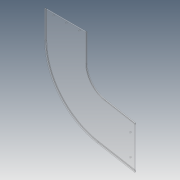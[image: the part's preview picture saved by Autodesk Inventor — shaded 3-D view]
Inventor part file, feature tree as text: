
AUTODESK INVENTOR PART (.ipt)
format: ipt  version: 2012 (Build 160160000, 160)  size: 145,408 bytes
history: native  units: in
note: dims shown in document units (in); Inventor stores cm internally (conversion verified against a paired STEP export)
features: extrude x2, hole x2, pattern_linear x2, sketch x2
ambient origin geometry x8: Origin, YZ Plane, XZ Plane, XY Plane, X Axis, Y Axis, Z Axis, Center Point
bodies: Solid1 (feature_tree)
feature tree (8):
  extrude  "Extrusion1"  Depth=9.625in
  extrude  "Extrusion3"  Depth=5.0in
  hole  "Hole1"  [1 undecoded]
  pattern_linear  "Rectangular Pattern1"  Spacing1=12.5in  [1 undecoded]
  hole  "Hole2"  [1 undecoded]
  pattern_linear  "Rectangular Pattern2"  Spacing1=0.25in  [1 undecoded]
  sketch  "Sketch1"  dims[d0=9.625in d1=9.625in]
  sketch  "Sketch3"  dims[d2=0.6871in d3=5.0in d4=14.625in d5=12.5in d6=20.75in d7=0.25in d8=0.0in d21=0.1875in d23=0.1875in d24=0.1875in d25=0.1875in d26=0.1875in d27=0.1875in d28=0.125in d29=0.125in d30=0.125in d31=0.125in d32=0.125in d33=0.0in d34=1.125in d35=14.875in d36=0.265in d37=0.75in d38=0.375in d39=0.25in d40=0.5635in d41=1.0in d42=0.8108in d43=0.7874in d45=5.0in d46=0.5in d47=1.75in d48=0.265in d49=0.75in d50=0.375in d51=0.25in d52=0.5635in d53=1.0in d54=0.8108in d55=1.1811in d57=3.0in]
note: 4 required parameter values undecoded (feature->parameter linkage not recoverable at this tier; creation-order binding heuristic only, values carry confidence <= 0.55)
